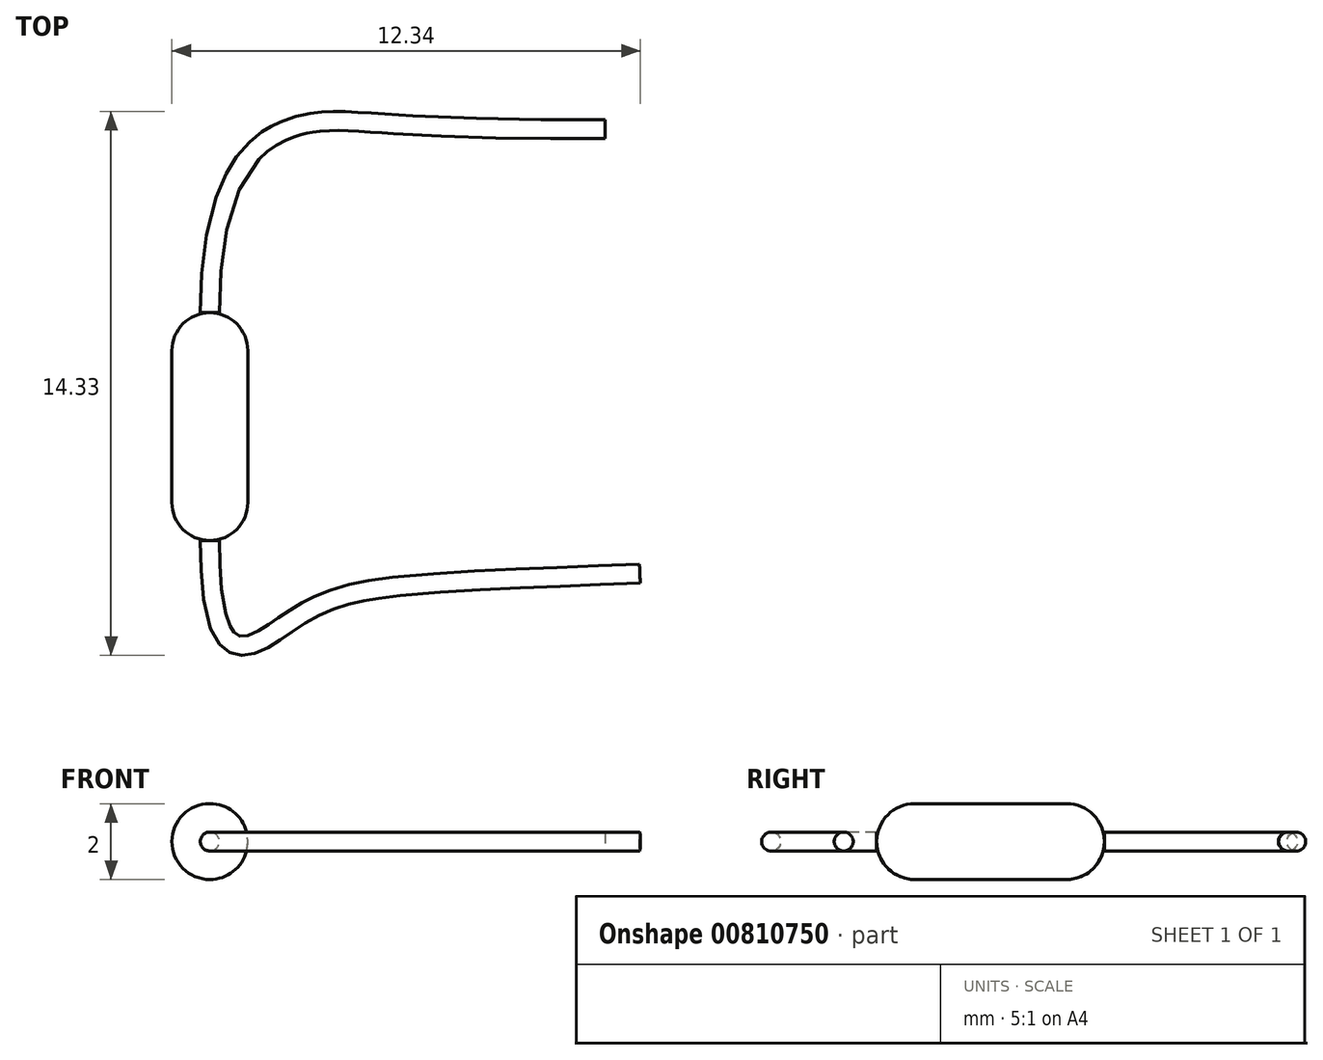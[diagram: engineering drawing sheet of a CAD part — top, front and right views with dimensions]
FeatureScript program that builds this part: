
annotation { "Feature Type Name" : "Feature", "Feature Type Description" : "" }
export const myFeature = defineFeature(function(context is Context, id is Id, definition is map)
    precondition{}
    {
        {
            var Q0;
            Q0=qCreatedBy(makeId("Front.planeOp"),FACE);
            var sketch = newSketch(context, id + "F0", { "sketchPlane" : qUnion([Q0])});
            skCircle(sketch, "E0", {"center": v(0, 0) * mm, "radius": 1 * mm});
            skSolve(sketch);
        }
        {
            var Q0;
            Q0=makeQuery(id+"F0.imprint","IMPRINT",FACE,{"disambiguationData":[TD([[makeQuery(id+"F0.imprint","IMPRINT",EDGE,{"derivedFrom":sQuery(id+"F0.wireOp",EDGE,"E0")}),1.0]])]});
            extrude(context, id + "F1", {"entities" : qUnion([Q0]), "depth" : 6 * mm, "offsetDistance" : 25 * mm});
        }
        {
            var Q0;
            Q0=makeQuery(id+"F1.opExtrude","CAP_FACE",FACE,{"disambiguationData":[OSD([sQuery(id+"F0.wireOp",EDGE,"E0")])],"isStart":false});
            var sketch = newSketch(context, id + "F2", { "sketchPlane" : qUnion([Q0])});
            skPoint(sketch, "E1", {"position": v(0, 0) * mm});
            skCircle(sketch, "E2", {"center": v(0, 0) * mm, "radius": 0.25 * mm});
            skSolve(sketch);
        }
        {
            var Q0;
            Q0=qCreatedBy(makeId("Top.planeOp"),FACE);
            var sketch = newSketch(context, id + "F3", { "sketchPlane" : qUnion([Q0])});
            skFitSpline(sketch, "E3", {"points": [v(0, 0) * mm, v(2.41, 4.95) * mm, v(10.41, 4.84) * mm], "startDerivative": vector(0, 25.93) * mm, "endDerivative": vector(33.84, 0.3) * mm});
            skFitSpline(sketch, "E4", {"points": [v(0, -6) * mm, v(2, -8.2) * mm, v(11.33, -6.87) * mm], "startDerivative": vector(0, -31.43) * mm, "endDerivative": vector(32.54, 1.35) * mm});
            skSolve(sketch);
        }
        {
            var Q0;
            Q0=makeQuery(id+"F1.opExtrude","CAP_FACE",FACE,{"disambiguationData":[OSD([sQuery(id+"F0.wireOp",EDGE,"E0")])],"isStart":true});
            var sketch = newSketch(context, id + "F4", { "sketchPlane" : qUnion([Q0])});
            skCircle(sketch, "E5", {"center": v(0, 0) * mm, "radius": 0.25 * mm});
            skSolve(sketch);
        }
        {
            var Q0;
            Q0=makeQuery(id+"F4.imprint","IMPRINT",FACE,{"disambiguationData":[TD([[makeQuery(id+"F4.imprint","IMPRINT",EDGE,{"derivedFrom":sQuery(id+"F4.wireOp",EDGE,"E5")}),1.0]])]});
            var Q1;
            Q1=sQuery(id+"F3.wireOp",EDGE,"E3");
            sweep(context, id + "F5", {"profiles" : qUnion([Q0]), "path" : qUnion([Q1])});
        }
        {
            var Q0;
            Q0=makeQuery(id+"F2.imprint","IMPRINT",FACE,{"disambiguationData":[TD([[makeQuery(id+"F2.imprint","IMPRINT",EDGE,{"derivedFrom":sQuery(id+"F2.wireOp",EDGE,"E2")}),1.0]])]});
            var Q1;
            Q1=sQuery(id+"F3.wireOp",EDGE,"E4");
            sweep(context, id + "F6", {"profiles" : qUnion([Q0]), "path" : qUnion([Q1])});
        }
        {
            var Q0;
            Q0=makeQuery(id+"F1.opExtrude","CAP_EDGE",EDGE,{"disambiguationData":[OSD([sQuery(id+"F0.wireOp",EDGE,"E0")])],"isStart":false});
            var Q1;
            Q1=makeQuery(id+"F1.opExtrude","CAP_EDGE",EDGE,{"disambiguationData":[OSD([sQuery(id+"F0.wireOp",EDGE,"E0")])],"isStart":true});
            fillet(context, id + "F7", {"entities" : qUnion([Q0, Q1]), "radius" : 1 * mm, "tangentPropagation" : true, "allowEdgeOverflow" : false});
        }
    });
